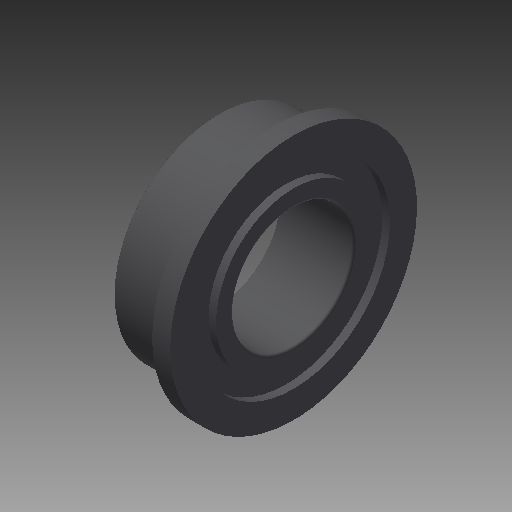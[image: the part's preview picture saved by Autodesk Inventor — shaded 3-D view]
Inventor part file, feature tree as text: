
AUTODESK INVENTOR PART (.ipt)
format: ipt  version: 2018 (Build 220112000, 112)  size: 183,808 bytes
history: native  units: mm
features: other x7, revolve x1, sketch x1
ambient origin geometry x8: Origin, YZ Plane, XZ Plane, XY Plane, X Axis, Y Axis, Z Axis, Center Point
bodies: Solid1 (feature_tree)
feature tree (9):
  revolve  "Revolution1"  [1 undecoded]
  other  "to_housing_XY"
  other  "to_housing_YZ"
  other  "to_housing_ZX"
  other  "to_housing_X"
  other  "to_housing_Y"
  other  "to_housing_Z"
  other  "to_housing_Center"
  sketch  "Sketch_1"  dims[d0=360.0deg d1=0.0mm]
note: 1 required parameter value undecoded (feature->parameter linkage not recoverable at this tier; creation-order binding heuristic only, values carry confidence <= 0.55)
